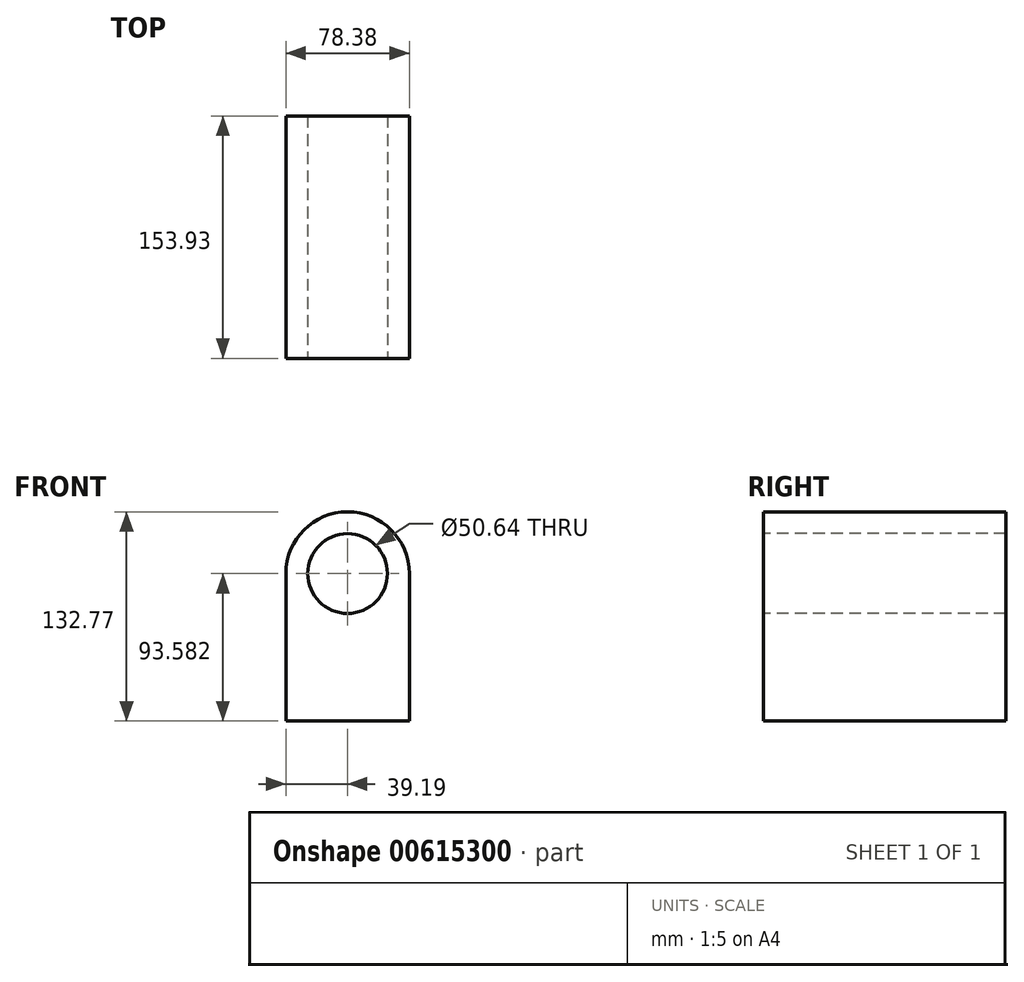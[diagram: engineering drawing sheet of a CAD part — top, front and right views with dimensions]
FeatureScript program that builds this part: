
annotation { "Feature Type Name" : "Feature", "Feature Type Description" : "" }
export const myFeature = defineFeature(function(context is Context, id is Id, definition is map)
    precondition{}
    {
        {
            var Q0;
            Q0=qCreatedBy(makeId("Front.planeOp"),FACE);
            var sketch = newSketch(context, id + "F0", { "sketchPlane" : qUnion([Q0])});
            skLineSegment(sketch, "E0.top", {"start": v(-39.2, -46.8) * mm, "end": v(39.2, -46.8) * mm});
            skLineSegment(sketch, "E0.left", {"start": v(-39.2, 46.8) * mm, "end": v(-39.2, -46.8) * mm});
            skLineSegment(sketch, "E0.right", {"start": v(39.2, 46.8) * mm, "end": v(39.2, -46.8) * mm});
            skPoint(sketch, "E0.middle", {"position": v(0, 0) * mm});
            skPoint(sketch, "E1.center.orphan", {"position": v(0, 46.8) * mm});
            skArc(sketch, "E2", {"start": v(39.2, 46.8) * mm, "mid": v(0, 85.98) * mm, "end": v(-39.2, 46.8) * mm});
            skCircle(sketch, "E3", {"center": v(0, 46.8) * mm, "radius": 25.32 * mm});
            skSolve(sketch);
        }
        {
            var Q0;
            Q0=makeQuery(id+"F0.imprint","IMPRINT",FACE,{"disambiguationData":[TD([[makeQuery(id+"F0.imprint","IMPRINT",EDGE,{"derivedFrom":sQuery(id+"F0.wireOp",EDGE,"E0.top")}),1.0]])]});
            extrude(context, id + "F1", {"entities" : qUnion([Q0]), "oppositeDirection" : true, "depth" : 77.98 * mm, "offsetDistance" : 25.4 * mm});
        }
        {
            var Q0;
            Q0=makeQuery(id+"F1.opExtrude","CAP_FACE",FACE,{"disambiguationData":[OSD([sQuery(id+"F0.wireOp",EDGE,"E0.top"),sQuery(id+"F0.wireOp",EDGE,"E0.left"),sQuery(id+"F0.wireOp",EDGE,"E0.right"),sQuery(id+"F0.wireOp",EDGE,"E2"),sQuery(id+"F0.wireOp",EDGE,"E3")])],"isStart":true});
            extrude(context, id + "F2", {"entities" : qUnion([Q0]), "operationType" : NewBodyOperationType.ADD, "depth" : 75.95 * mm, "offsetDistance" : 25.4 * mm});
        }
    });
